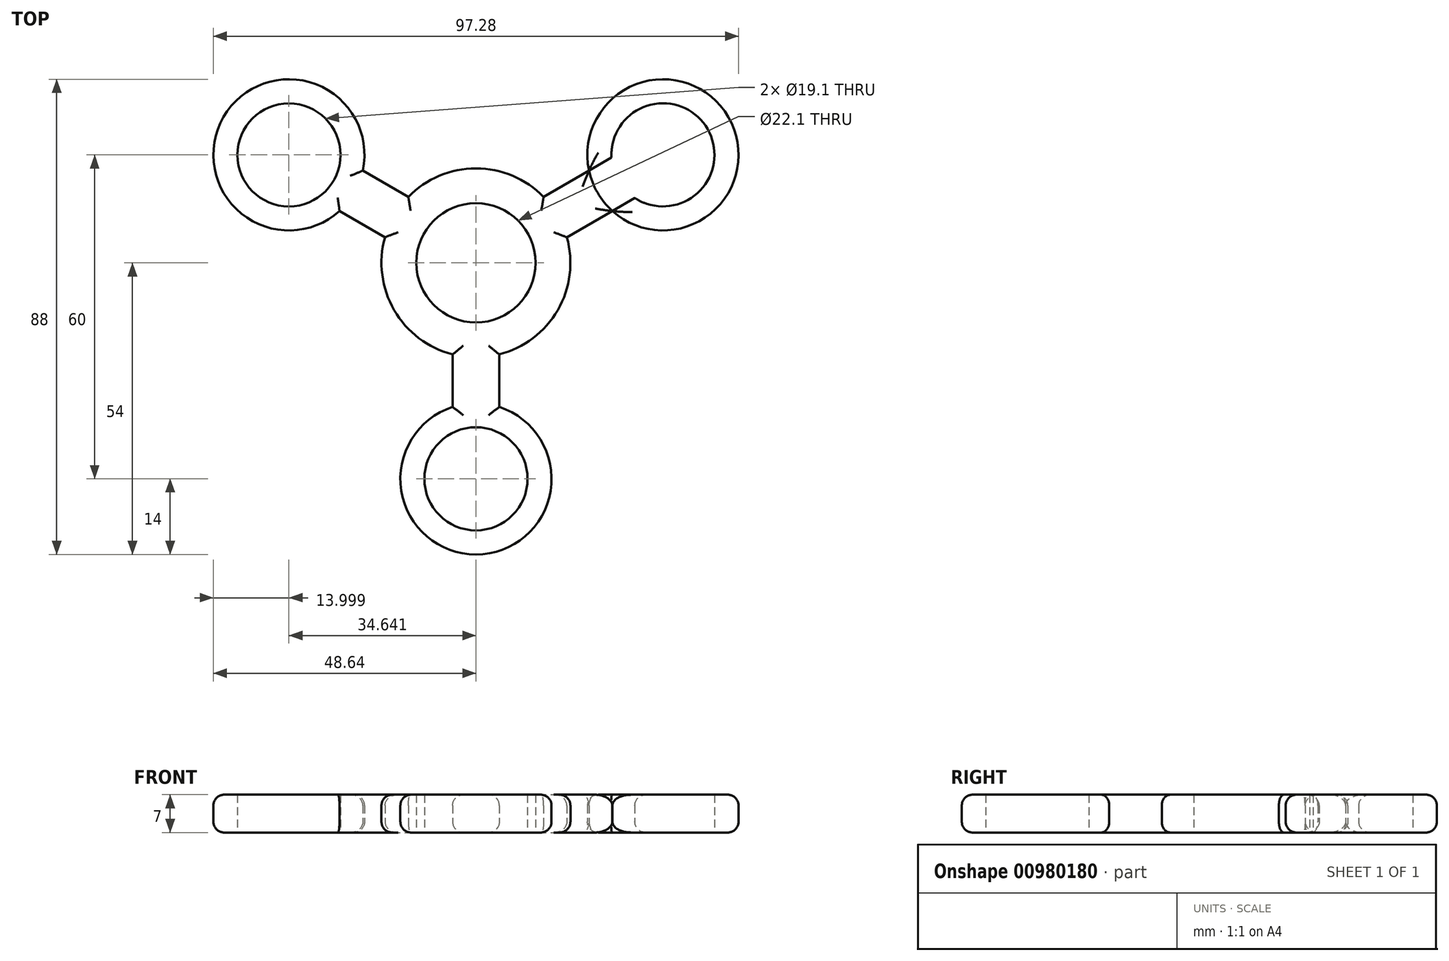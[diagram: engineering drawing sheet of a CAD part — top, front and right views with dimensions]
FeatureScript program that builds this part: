
annotation { "Feature Type Name" : "Feature", "Feature Type Description" : "" }
export const myFeature = defineFeature(function(context is Context, id is Id, definition is map)
    precondition{}
    {
        {
            var Q0;
            Q0=qCreatedBy(makeId("Top.planeOp"),FACE);
            var sketch = newSketch(context, id + "F0", { "sketchPlane" : qUnion([Q0])});
            skCircle(sketch, "E0", {"center": v(0, 0) * mm, "radius": 11.05 * mm});
            skCircle(sketch, "E1", {"center": v(0, 0) * mm, "radius": 17.5 * mm});
            skLineSegment(sketch, "E2", {"start": v(0, 0) * mm, "end": v(34.64, 20) * mm});
            skLineSegment(sketch, "E3", {"start": v(34.64, 20) * mm, "end": v(0, 0) * mm});
            skLineSegment(sketch, "E4", {"start": v(0, 0) * mm, "end": v(-34.64, 20) * mm});
            skLineSegment(sketch, "E5", {"start": v(0, 0) * mm, "end": v(0, -40) * mm});
            skCircle(sketch, "E6", {"center": v(34.64, 20) * mm, "radius": 9.55 * mm});
            skCircle(sketch, "E7", {"center": v(34.64, 20) * mm, "radius": 14 * mm});
            skCircle(sketch, "E8", {"center": v(-34.64, 20) * mm, "radius": 9.55 * mm});
            skCircle(sketch, "E9", {"center": v(-34.64, 20) * mm, "radius": 14 * mm});
            skCircle(sketch, "E10", {"center": v(0, -40) * mm, "radius": 9.55 * mm});
            skCircle(sketch, "E11", {"center": v(0, -40) * mm, "radius": 14 * mm});
            skLineSegment(sketch, "E12", {"start": v(0, 0) * mm, "end": v(-4.33, -2.5) * mm});
            skLineSegment(sketch, "E13", {"start": v(0, 0) * mm, "end": v(4.33, -2.5) * mm});
            skLineSegment(sketch, "E14", {"start": v(0, 0) * mm, "end": v(0, 5) * mm});
            skLineSegment(sketch, "E15", {"start": v(4.33, -2.5) * mm, "end": v(36.91, 16.31) * mm});
            skLineSegment(sketch, "E16", {"start": v(0, 5) * mm, "end": v(31.97, 23.46) * mm});
            skLineSegment(sketch, "E17", {"start": v(4.33, -2.5) * mm, "end": v(4.33, -38.55) * mm});
            skLineSegment(sketch, "E18", {"start": v(-4.33, -2.5) * mm, "end": v(-4.33, -37.35) * mm});
            skLineSegment(sketch, "E19", {"start": v(0, 5) * mm, "end": v(-32.3, 23.64) * mm});
            skLineSegment(sketch, "E20", {"start": v(-4.33, -2.5) * mm, "end": v(-36.69, 16.18) * mm});
            skSolve(sketch);
        }
        {
            var Q0;
            {var subQ0=sQuery(id+"F0.wireOp",EDGE,"E16");var subQ1=sQuery(id+"F0.wireOp",EDGE,"E0");var subQ2=makeQuery(id+"F0.imprint","INTERSECT",VERTEX,{"derivedFrom":[subQ1,subQ0]});Q0=makeQuery(id+"F0.imprint","IMPRINT",FACE,{"disambiguationData":[TD([[makeQuery(id+"F0.imprint","IMPRINT",EDGE,{"disambiguationData":[TD([[subQ2,-1.0]])],"derivedFrom":subQ1}),-1.0]])]});}
            var Q1;
            {var subQ0=sQuery(id+"F0.wireOp",EDGE,"E3");var subQ1=sQuery(id+"F0.wireOp",EDGE,"E0");var subQ2=makeQuery(id+"F0.imprint","INTERSECT",VERTEX,{"derivedFrom":[subQ1,subQ0]});Q1=makeQuery(id+"F0.imprint","IMPRINT",FACE,{"disambiguationData":[TD([[makeQuery(id+"F0.imprint","IMPRINT",EDGE,{"disambiguationData":[TD([[subQ2,-1.0]])],"derivedFrom":subQ1}),-1.0]])]});}
            var Q2;
            {var subQ0=sQuery(id+"F0.wireOp",EDGE,"E3");var subQ1=sQuery(id+"F0.wireOp",EDGE,"E0");var subQ2=makeQuery(id+"F0.imprint","INTERSECT",VERTEX,{"derivedFrom":[subQ1,subQ0]});Q2=makeQuery(id+"F0.imprint","IMPRINT",FACE,{"disambiguationData":[TD([[makeQuery(id+"F0.imprint","IMPRINT",EDGE,{"disambiguationData":[TD([[subQ2,1.0]])],"derivedFrom":subQ1}),-1.0]])]});}
            var Q3;
            {var subQ0=sQuery(id+"F0.wireOp",EDGE,"E16");var subQ1=sQuery(id+"F0.wireOp",EDGE,"E1");var subQ2=makeQuery(id+"F0.imprint","INTERSECT",VERTEX,{"derivedFrom":[subQ1,subQ0]});Q3=makeQuery(id+"F0.imprint","IMPRINT",FACE,{"disambiguationData":[TD([[makeQuery(id+"F0.imprint","IMPRINT",EDGE,{"disambiguationData":[TD([[subQ2,1.0]])],"derivedFrom":subQ1}),-1.0]])]});}
            var Q4;
            {var subQ0=sQuery(id+"F0.wireOp",EDGE,"E15");var subQ1=sQuery(id+"F0.wireOp",EDGE,"E1");var subQ2=makeQuery(id+"F0.imprint","INTERSECT",VERTEX,{"derivedFrom":[subQ1,subQ0]});Q4=makeQuery(id+"F0.imprint","IMPRINT",FACE,{"disambiguationData":[TD([[makeQuery(id+"F0.imprint","IMPRINT",EDGE,{"disambiguationData":[TD([[subQ2,-1.0]])],"derivedFrom":subQ1}),-1.0]])]});}
            var Q5;
            {var subQ0=sQuery(id+"F0.wireOp",EDGE,"E6");var subQ1=sQuery(id+"F0.wireOp",EDGE,"E3");var subQ2=makeQuery(id+"F0.imprint","INTERSECT",VERTEX,{"derivedFrom":[subQ1,subQ0]});Q5=makeQuery(id+"F0.imprint","IMPRINT",FACE,{"disambiguationData":[TD([[makeQuery(id+"F0.imprint","IMPRINT",EDGE,{"disambiguationData":[TD([[subQ2,-1.0]])],"derivedFrom":subQ1}),-1.0]])]});}
            var Q6;
            {var subQ0=sQuery(id+"F0.wireOp",EDGE,"E6");var subQ1=sQuery(id+"F0.wireOp",EDGE,"E3");var subQ2=makeQuery(id+"F0.imprint","INTERSECT",VERTEX,{"derivedFrom":[subQ1,subQ0]});Q6=makeQuery(id+"F0.imprint","IMPRINT",FACE,{"disambiguationData":[TD([[makeQuery(id+"F0.imprint","IMPRINT",EDGE,{"disambiguationData":[TD([[subQ2,-1.0]])],"derivedFrom":subQ1}),1.0]])]});}
            var Q7;
            {var subQ0=sQuery(id+"F0.wireOp",EDGE,"E16");var subQ1=sQuery(id+"F0.wireOp",EDGE,"E6");var subQ2=makeQuery(id+"F0.imprint","INTERSECT",VERTEX,{"derivedFrom":[subQ1,subQ0]});Q7=makeQuery(id+"F0.imprint","IMPRINT",FACE,{"disambiguationData":[TD([[makeQuery(id+"F0.imprint","IMPRINT",EDGE,{"disambiguationData":[TD([[subQ2,1.0]])],"derivedFrom":subQ1}),-1.0]])]});}
            var Q8;
            {var subQ0=sQuery(id+"F0.wireOp",EDGE,"E15");var subQ1=sQuery(id+"F0.wireOp",EDGE,"E0");var subQ2=makeQuery(id+"F0.imprint","INTERSECT",VERTEX,{"derivedFrom":[subQ1,subQ0]});Q8=makeQuery(id+"F0.imprint","IMPRINT",FACE,{"disambiguationData":[TD([[makeQuery(id+"F0.imprint","IMPRINT",EDGE,{"disambiguationData":[TD([[subQ2,1.0]])],"derivedFrom":subQ1}),-1.0]])]});}
            var Q9;
            {var subQ0=sQuery(id+"F0.wireOp",EDGE,"E18");var subQ1=sQuery(id+"F0.wireOp",EDGE,"E0");var subQ2=makeQuery(id+"F0.imprint","INTERSECT",VERTEX,{"derivedFrom":[subQ1,subQ0]});Q9=makeQuery(id+"F0.imprint","IMPRINT",FACE,{"disambiguationData":[TD([[makeQuery(id+"F0.imprint","IMPRINT",EDGE,{"disambiguationData":[TD([[subQ2,-1.0]])],"derivedFrom":subQ1}),-1.0]])]});}
            var Q10;
            {var subQ0=sQuery(id+"F0.wireOp",EDGE,"E5");var subQ1=sQuery(id+"F0.wireOp",EDGE,"E0");var subQ2=makeQuery(id+"F0.imprint","INTERSECT",VERTEX,{"derivedFrom":[subQ1,subQ0]});Q10=makeQuery(id+"F0.imprint","IMPRINT",FACE,{"disambiguationData":[TD([[makeQuery(id+"F0.imprint","IMPRINT",EDGE,{"disambiguationData":[TD([[subQ2,-1.0]])],"derivedFrom":subQ1}),-1.0]])]});}
            var Q11;
            {var subQ0=sQuery(id+"F0.wireOp",EDGE,"E20");var subQ1=sQuery(id+"F0.wireOp",EDGE,"E0");var subQ2=makeQuery(id+"F0.imprint","INTERSECT",VERTEX,{"derivedFrom":[subQ1,subQ0]});Q11=makeQuery(id+"F0.imprint","IMPRINT",FACE,{"disambiguationData":[TD([[makeQuery(id+"F0.imprint","IMPRINT",EDGE,{"disambiguationData":[TD([[subQ2,-1.0]])],"derivedFrom":subQ1}),-1.0]])]});}
            var Q12;
            {var subQ0=sQuery(id+"F0.wireOp",EDGE,"E4");var subQ1=sQuery(id+"F0.wireOp",EDGE,"E0");var subQ2=makeQuery(id+"F0.imprint","INTERSECT",VERTEX,{"derivedFrom":[subQ1,subQ0]});Q12=makeQuery(id+"F0.imprint","IMPRINT",FACE,{"disambiguationData":[TD([[makeQuery(id+"F0.imprint","IMPRINT",EDGE,{"disambiguationData":[TD([[subQ2,-1.0]])],"derivedFrom":subQ1}),-1.0]])]});}
            var Q13;
            {var subQ0=sQuery(id+"F0.wireOp",EDGE,"E19");var subQ1=sQuery(id+"F0.wireOp",EDGE,"E0");var subQ2=makeQuery(id+"F0.imprint","INTERSECT",VERTEX,{"derivedFrom":[subQ1,subQ0]});Q13=makeQuery(id+"F0.imprint","IMPRINT",FACE,{"disambiguationData":[TD([[makeQuery(id+"F0.imprint","IMPRINT",EDGE,{"disambiguationData":[TD([[subQ2,-1.0]])],"derivedFrom":subQ1}),-1.0]])]});}
            var Q14;
            {var subQ0=sQuery(id+"F0.wireOp",EDGE,"E19");var subQ1=sQuery(id+"F0.wireOp",EDGE,"E1");var subQ2=makeQuery(id+"F0.imprint","INTERSECT",VERTEX,{"derivedFrom":[subQ1,subQ0]});Q14=makeQuery(id+"F0.imprint","IMPRINT",FACE,{"disambiguationData":[TD([[makeQuery(id+"F0.imprint","IMPRINT",EDGE,{"disambiguationData":[TD([[subQ2,-1.0]])],"derivedFrom":subQ1}),-1.0]])]});}
            var Q15;
            {var subQ0=sQuery(id+"F0.wireOp",EDGE,"E20");var subQ1=sQuery(id+"F0.wireOp",EDGE,"E1");var subQ2=makeQuery(id+"F0.imprint","INTERSECT",VERTEX,{"derivedFrom":[subQ1,subQ0]});Q15=makeQuery(id+"F0.imprint","IMPRINT",FACE,{"disambiguationData":[TD([[makeQuery(id+"F0.imprint","IMPRINT",EDGE,{"disambiguationData":[TD([[subQ2,1.0]])],"derivedFrom":subQ1}),-1.0]])]});}
            var Q16;
            {var subQ0=sQuery(id+"F0.wireOp",EDGE,"E8");var subQ1=sQuery(id+"F0.wireOp",EDGE,"E4");var subQ2=makeQuery(id+"F0.imprint","INTERSECT",VERTEX,{"derivedFrom":[subQ1,subQ0]});Q16=makeQuery(id+"F0.imprint","IMPRINT",FACE,{"disambiguationData":[TD([[makeQuery(id+"F0.imprint","IMPRINT",EDGE,{"disambiguationData":[TD([[subQ2,1.0]])],"derivedFrom":subQ1}),1.0]])]});}
            var Q17;
            {var subQ0=sQuery(id+"F0.wireOp",EDGE,"E8");var subQ1=sQuery(id+"F0.wireOp",EDGE,"E4");var subQ2=makeQuery(id+"F0.imprint","INTERSECT",VERTEX,{"derivedFrom":[subQ1,subQ0]});Q17=makeQuery(id+"F0.imprint","IMPRINT",FACE,{"disambiguationData":[TD([[makeQuery(id+"F0.imprint","IMPRINT",EDGE,{"disambiguationData":[TD([[subQ2,1.0]])],"derivedFrom":subQ1}),-1.0]])]});}
            var Q18;
            {var subQ0=sQuery(id+"F0.wireOp",EDGE,"E20");var subQ1=sQuery(id+"F0.wireOp",EDGE,"E8");var subQ2=makeQuery(id+"F0.imprint","INTERSECT",VERTEX,{"derivedFrom":[subQ1,subQ0]});Q18=makeQuery(id+"F0.imprint","IMPRINT",FACE,{"disambiguationData":[TD([[makeQuery(id+"F0.imprint","IMPRINT",EDGE,{"disambiguationData":[TD([[subQ2,1.0]])],"derivedFrom":subQ1}),-1.0]])]});}
            var Q19;
            {var subQ0=sQuery(id+"F0.wireOp",EDGE,"E18");var subQ1=sQuery(id+"F0.wireOp",EDGE,"E1");var subQ2=makeQuery(id+"F0.imprint","INTERSECT",VERTEX,{"derivedFrom":[subQ1,subQ0]});Q19=makeQuery(id+"F0.imprint","IMPRINT",FACE,{"disambiguationData":[TD([[makeQuery(id+"F0.imprint","IMPRINT",EDGE,{"disambiguationData":[TD([[subQ2,-1.0]])],"derivedFrom":subQ1}),-1.0]])]});}
            var Q20;
            {var subQ0=sQuery(id+"F0.wireOp",EDGE,"E17");var subQ1=sQuery(id+"F0.wireOp",EDGE,"E1");var subQ2=makeQuery(id+"F0.imprint","INTERSECT",VERTEX,{"derivedFrom":[subQ1,subQ0]});Q20=makeQuery(id+"F0.imprint","IMPRINT",FACE,{"disambiguationData":[TD([[makeQuery(id+"F0.imprint","IMPRINT",EDGE,{"disambiguationData":[TD([[subQ2,1.0]])],"derivedFrom":subQ1}),-1.0]])]});}
            var Q21;
            {var subQ0=sQuery(id+"F0.wireOp",EDGE,"E10");var subQ1=sQuery(id+"F0.wireOp",EDGE,"E5");var subQ2=makeQuery(id+"F0.imprint","INTERSECT",VERTEX,{"derivedFrom":[subQ1,subQ0]});Q21=makeQuery(id+"F0.imprint","IMPRINT",FACE,{"disambiguationData":[TD([[makeQuery(id+"F0.imprint","IMPRINT",EDGE,{"disambiguationData":[TD([[subQ2,1.0]])],"derivedFrom":subQ1}),1.0]])]});}
            var Q22;
            {var subQ0=sQuery(id+"F0.wireOp",EDGE,"E10");var subQ1=sQuery(id+"F0.wireOp",EDGE,"E5");var subQ2=makeQuery(id+"F0.imprint","INTERSECT",VERTEX,{"derivedFrom":[subQ1,subQ0]});Q22=makeQuery(id+"F0.imprint","IMPRINT",FACE,{"disambiguationData":[TD([[makeQuery(id+"F0.imprint","IMPRINT",EDGE,{"disambiguationData":[TD([[subQ2,1.0]])],"derivedFrom":subQ1}),-1.0]])]});}
            var Q23;
            {var subQ0=sQuery(id+"F0.wireOp",EDGE,"E17");var subQ1=sQuery(id+"F0.wireOp",EDGE,"E10");var subQ2=makeQuery(id+"F0.imprint","INTERSECT",VERTEX,{"derivedFrom":[subQ1,subQ0]});Q23=makeQuery(id+"F0.imprint","IMPRINT",FACE,{"disambiguationData":[TD([[makeQuery(id+"F0.imprint","IMPRINT",EDGE,{"disambiguationData":[TD([[subQ2,1.0]])],"derivedFrom":subQ1}),-1.0]])]});}
            extrude(context, id + "F1", {"entities" : qUnion([Q0, Q1, Q2, Q3, Q4, Q5, Q6, Q7, Q8, Q9, Q10, Q11, Q12, Q13, Q14, Q15, Q16, Q17, Q18, Q19, Q20, Q21, Q22, Q23]), "depth" : 7 * mm, "offsetDistance" : 25 * mm});
        }
        {
            var Q0;
            {var subQ0=sQuery(id+"F0.wireOp",EDGE,"E1");Q0=makeQuery(id+"F1.opExtrude","CAP_EDGE",EDGE,{"disambiguationData":[OSD([subQ0]),TDD([makeQuery(id+"F0.imprint","IMPRINT",EDGE,{"disambiguationData":[TD([[makeQuery(id+"F0.imprint","INTERSECT",VERTEX,{"derivedFrom":[subQ0,sQuery(id+"F0.wireOp",EDGE,"E15")]}),1.0]])],"derivedFrom":subQ0})])],"isStart":false});}
            var Q1;
            Q1=makeQuery(id+"F1.opExtrude","CAP_EDGE",EDGE,{"disambiguationData":[OSD([sQuery(id+"F0.wireOp",EDGE,"E17")])],"isStart":false});
            var Q2;
            Q2=makeQuery(id+"F1.opExtrude","CAP_EDGE",EDGE,{"disambiguationData":[OSD([sQuery(id+"F0.wireOp",EDGE,"E18")])],"isStart":false});
            var Q3;
            Q3=makeQuery(id+"F1.opExtrude","CAP_EDGE",EDGE,{"disambiguationData":[OSD([sQuery(id+"F0.wireOp",EDGE,"E11")])],"isStart":false});
            var Q4;
            {var subQ0=sQuery(id+"F0.wireOp",EDGE,"E1");Q4=makeQuery(id+"F1.opExtrude","CAP_EDGE",EDGE,{"disambiguationData":[OSD([subQ0]),TDD([makeQuery(id+"F0.imprint","IMPRINT",EDGE,{"disambiguationData":[TD([[makeQuery(id+"F0.imprint","INTERSECT",VERTEX,{"derivedFrom":[subQ0,sQuery(id+"F0.wireOp",EDGE,"E20")]}),-1.0]])],"derivedFrom":subQ0})])],"isStart":false});}
            var Q5;
            Q5=makeQuery(id+"F1.opExtrude","CAP_EDGE",EDGE,{"disambiguationData":[OSD([sQuery(id+"F0.wireOp",EDGE,"E20")])],"isStart":false});
            var Q6;
            Q6=makeQuery(id+"F1.opExtrude","CAP_EDGE",EDGE,{"disambiguationData":[OSD([sQuery(id+"F0.wireOp",EDGE,"E9")])],"isStart":false});
            var Q7;
            Q7=makeQuery(id+"F1.opExtrude","CAP_EDGE",EDGE,{"disambiguationData":[OSD([sQuery(id+"F0.wireOp",EDGE,"E19")])],"isStart":false});
            var Q8;
            {var subQ0=sQuery(id+"F0.wireOp",EDGE,"E1");Q8=makeQuery(id+"F1.opExtrude","CAP_EDGE",EDGE,{"disambiguationData":[OSD([subQ0]),TDD([makeQuery(id+"F0.imprint","IMPRINT",EDGE,{"disambiguationData":[TD([[makeQuery(id+"F0.imprint","INTERSECT",VERTEX,{"derivedFrom":[subQ0,sQuery(id+"F0.wireOp",EDGE,"E16")]}),-1.0]])],"derivedFrom":subQ0})])],"isStart":false});}
            var Q9;
            Q9=makeQuery(id+"F1.opExtrude","CAP_EDGE",EDGE,{"disambiguationData":[OSD([sQuery(id+"F0.wireOp",EDGE,"E16")])],"isStart":false});
            var Q10;
            Q10=makeQuery(id+"F1.opExtrude","CAP_EDGE",EDGE,{"disambiguationData":[OSD([sQuery(id+"F0.wireOp",EDGE,"E7")])],"isStart":false});
            var Q11;
            Q11=makeQuery(id+"F1.opExtrude","CAP_EDGE",EDGE,{"disambiguationData":[OSD([sQuery(id+"F0.wireOp",EDGE,"E15")])],"isStart":false});
            var Q12;
            Q12=makeQuery(id+"F1.opExtrude","CAP_EDGE",EDGE,{"disambiguationData":[OSD([sQuery(id+"F0.wireOp",EDGE,"E11")])],"isStart":true});
            var Q13;
            Q13=makeQuery(id+"F1.opExtrude","CAP_EDGE",EDGE,{"disambiguationData":[OSD([sQuery(id+"F0.wireOp",EDGE,"E17")])],"isStart":true});
            var Q14;
            Q14=makeQuery(id+"F1.opExtrude","CAP_EDGE",EDGE,{"disambiguationData":[OSD([sQuery(id+"F0.wireOp",EDGE,"E18")])],"isStart":true});
            var Q15;
            {var subQ0=sQuery(id+"F0.wireOp",EDGE,"E1");Q15=makeQuery(id+"F1.opExtrude","CAP_EDGE",EDGE,{"disambiguationData":[OSD([subQ0]),TDD([makeQuery(id+"F0.imprint","IMPRINT",EDGE,{"disambiguationData":[TD([[makeQuery(id+"F0.imprint","INTERSECT",VERTEX,{"derivedFrom":[subQ0,sQuery(id+"F0.wireOp",EDGE,"E20")]}),-1.0]])],"derivedFrom":subQ0})])],"isStart":true});}
            var Q16;
            Q16=makeQuery(id+"F1.opExtrude","CAP_EDGE",EDGE,{"disambiguationData":[OSD([sQuery(id+"F0.wireOp",EDGE,"E20")])],"isStart":true});
            var Q17;
            Q17=makeQuery(id+"F1.opExtrude","CAP_EDGE",EDGE,{"disambiguationData":[OSD([sQuery(id+"F0.wireOp",EDGE,"E19")])],"isStart":true});
            var Q18;
            Q18=makeQuery(id+"F1.opExtrude","CAP_EDGE",EDGE,{"disambiguationData":[OSD([sQuery(id+"F0.wireOp",EDGE,"E9")])],"isStart":true});
            var Q19;
            Q19=makeQuery(id+"F1.opExtrude","CAP_EDGE",EDGE,{"disambiguationData":[OSD([sQuery(id+"F0.wireOp",EDGE,"E16")])],"isStart":true});
            var Q20;
            {var subQ0=sQuery(id+"F0.wireOp",EDGE,"E1");Q20=makeQuery(id+"F1.opExtrude","CAP_EDGE",EDGE,{"disambiguationData":[OSD([subQ0]),TDD([makeQuery(id+"F0.imprint","IMPRINT",EDGE,{"disambiguationData":[TD([[makeQuery(id+"F0.imprint","INTERSECT",VERTEX,{"derivedFrom":[subQ0,sQuery(id+"F0.wireOp",EDGE,"E16")]}),-1.0]])],"derivedFrom":subQ0})])],"isStart":true});}
            var Q21;
            Q21=makeQuery(id+"F1.opExtrude","CAP_EDGE",EDGE,{"disambiguationData":[OSD([sQuery(id+"F0.wireOp",EDGE,"E7")])],"isStart":true});
            var Q22;
            {var subQ0=sQuery(id+"F0.wireOp",EDGE,"E1");Q22=makeQuery(id+"F1.opExtrude","CAP_EDGE",EDGE,{"disambiguationData":[OSD([subQ0]),TDD([makeQuery(id+"F0.imprint","IMPRINT",EDGE,{"disambiguationData":[TD([[makeQuery(id+"F0.imprint","INTERSECT",VERTEX,{"derivedFrom":[subQ0,sQuery(id+"F0.wireOp",EDGE,"E15")]}),1.0]])],"derivedFrom":subQ0})])],"isStart":true});}
            var Q23;
            Q23=makeQuery(id+"F1.opExtrude","CAP_EDGE",EDGE,{"disambiguationData":[OSD([sQuery(id+"F0.wireOp",EDGE,"E15")])],"isStart":true});
            fillet(context, id + "F2", {"entities" : qUnion([Q0, Q1, Q2, Q3, Q4, Q5, Q6, Q7, Q8, Q9, Q10, Q11, Q12, Q13, Q14, Q15, Q16, Q17, Q18, Q19, Q20, Q21, Q22, Q23]), "radius" : 2 * mm, "tangentPropagation" : true, "allowEdgeOverflow" : false});
        }
    });
